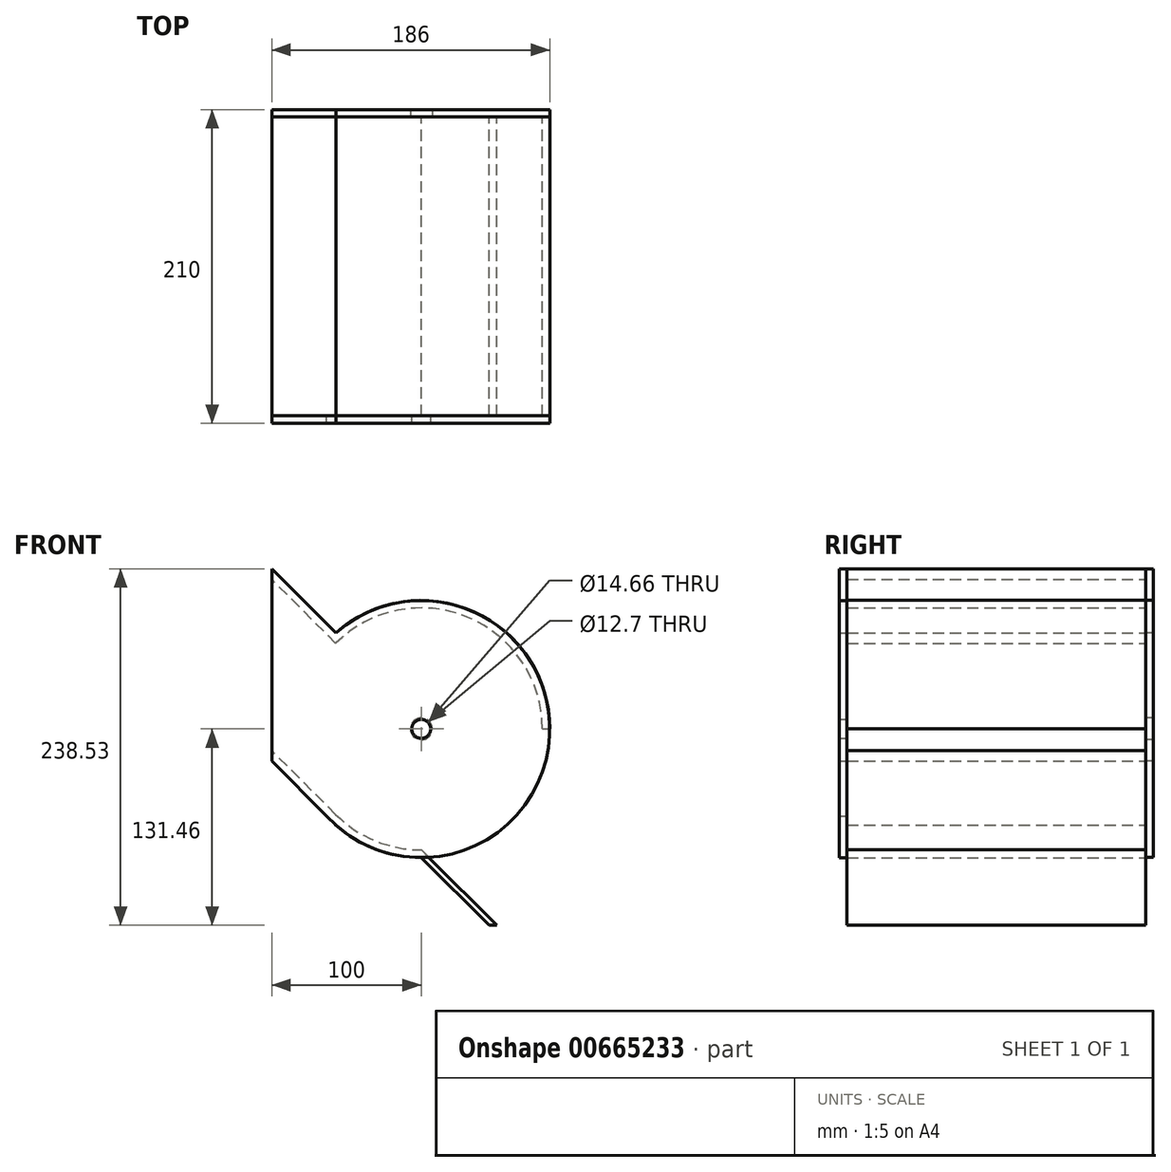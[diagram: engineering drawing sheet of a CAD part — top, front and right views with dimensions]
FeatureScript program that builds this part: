
annotation { "Feature Type Name" : "Feature", "Feature Type Description" : "" }
export const myFeature = defineFeature(function(context is Context, id is Id, definition is map)
    precondition{}
    {
        {
            var Q0;
            Q0=qCreatedBy(makeId("Front.planeOp"),FACE);
            var sketch = newSketch(context, id + "F0", { "sketchPlane" : qUnion([Q0])});
            skArc(sketch, "E0", {"start": v(81, 0) * mm, "mid": v(31, 74.83) * mm, "end": v(-57.28, 57.28) * mm});
            skLineSegment(sketch, "E1", {"start": v(0, 0) * mm, "end": v(0, -81) * mm});
            skPoint(sketch, "E2.visualSharp", {"position": v(0, -81) * mm});
            skArc(sketch, "E3", {"start": v(0, -81) * mm, "mid": v(-31, -74.83) * mm, "end": v(-57.28, -57.28) * mm});
            skLineSegment(sketch, "E4", {"start": v(-57.28, -57.28) * mm, "end": v(-100, -14.55) * mm});
            skLineSegment(sketch, "E5", {"start": v(81, 0) * mm, "end": v(86, 0) * mm});
            skArc(sketch, "E6", {"start": v(86, 0) * mm, "mid": v(35.2, 78.46) * mm, "end": v(-57.17, 64.24) * mm});
            skLineSegment(sketch, "E7", {"start": v(-100, -21.62) * mm, "end": v(-57.28, -64.35) * mm});
            skArc(sketch, "E8", {"start": v(-57.28, -64.35) * mm, "mid": v(-30.64, -80.51) * mm, "end": v(0, -86.15) * mm});
            skLineSegment(sketch, "E9", {"start": v(0, -81) * mm, "end": v(50.46, -131.46) * mm});
            skLineSegment(sketch, "E10", {"start": v(0, -86.15) * mm, "end": v(45.32, -131.46) * mm});
            skLineSegment(sketch, "E11", {"start": v(45.32, -131.46) * mm, "end": v(50.46, -131.46) * mm});
            skLineSegment(sketch, "E12", {"start": v(0, 0) * mm, "end": v(-100, 0) * mm, "construction": true});
            skLineSegment(sketch, "E13", {"start": v(-100, 0) * mm, "end": v(-100, 100) * mm, "construction": true});
            skLineSegment(sketch, "E14", {"start": v(-100, 100) * mm, "end": v(-100, 107.07) * mm});
            skLineSegment(sketch, "E15", {"start": v(-100, 107.07) * mm, "end": v(-57.17, 64.24) * mm});
            skLineSegment(sketch, "E16", {"start": v(-57.28, 57.28) * mm, "end": v(-100, 100) * mm});
            skLineSegment(sketch, "E17", {"start": v(-100, 0) * mm, "end": v(-100, -31.16) * mm, "construction": true});
            skLineSegment(sketch, "E18", {"start": v(-100, -14.55) * mm, "end": v(-100, -21.62) * mm});
            skSolve(sketch);
        }
        {
            var Q0;
            Q0=qSketchRegion(id+"F0",true);
            extrude(context, id + "F1", {"entities" : qUnion([Q0]), "depth" : 200 * mm});
        }
        {
            var Q0;
            Q0=qCreatedBy(makeId("Front.planeOp"),FACE);
            var sketch = newSketch(context, id + "F2", { "sketchPlane" : qUnion([Q0])});
            skCircle(sketch, "E19", {"center": v(0, 0) * mm, "radius": 86 * mm});
            skLineSegment(sketch, "E20", {"start": v(0, 0) * mm, "end": v(-100, 0) * mm});
            skLineSegment(sketch, "E21", {"start": v(-100, 0) * mm, "end": v(-100, -43.24) * mm, "construction": true});
            skLineSegment(sketch, "E22", {"start": v(-100, 0) * mm, "end": v(-100, 141.76) * mm, "construction": true});
            skLineSegment(sketch, "E23", {"start": v(-57.18, 64.24) * mm, "end": v(-100, 107.06) * mm});
            skLineSegment(sketch, "E24", {"start": v(-100, -21.62) * mm, "end": v(-60.81, -60.81) * mm});
            skLineSegment(sketch, "E25", {"start": v(-100, 107.06) * mm, "end": v(-100, -21.62) * mm});
            skLineSegment(sketch, "E26", {"start": v(0, 0) * mm, "end": v(0, -86) * mm});
            skLineSegment(sketch, "E27", {"start": v(0, 0) * mm, "end": v(-60.81, -60.81) * mm, "construction": true});
            skCircle(sketch, "E28", {"center": v(0, 0) * mm, "radius": 7.33 * mm});
            skSolve(sketch);
        }
        {
            var Q0;
            Q0=qSketchRegion(id+"F2",true);
            extrude(context, id + "F3", {"entities" : qUnion([Q0]), "oppositeDirection" : true, "depth" : 5 * mm});
        }
        {
            var Q0;
            Q0=qCreatedBy(makeId("Front.planeOp"),FACE);
            cPlane(context, id + "F4", {"entities" : qUnion([Q0]), "cplaneType" : CPlaneType.OFFSET, "offset" : 200 * mm, "width" : 150 * mm, "height" : 150 * mm});
        }
        {
            var Q0;
            Q0=qCreatedBy(id+"F4.planeOp",FACE);
            var sketch = newSketch(context, id + "F5", { "sketchPlane" : qUnion([Q0])});
            skCircle(sketch, "E29", {"center": v(0, -0.12) * mm, "radius": 86 * mm});
            skLineSegment(sketch, "E30", {"start": v(0, -0.12) * mm, "end": v(-100, -0.12) * mm});
            skLineSegment(sketch, "E31", {"start": v(-100, -0.12) * mm, "end": v(-100, -43.14) * mm, "construction": true});
            skLineSegment(sketch, "E32", {"start": v(-100, -0.12) * mm, "end": v(-100, 130.25) * mm, "construction": true});
            skLineSegment(sketch, "E33", {"start": v(-57.12, 64.18) * mm, "end": v(-100, 107.06) * mm});
            skLineSegment(sketch, "E34", {"start": v(-100, -21.63) * mm, "end": v(-58.14, -63.48) * mm});
            skLineSegment(sketch, "E35", {"start": v(-100, 107.06) * mm, "end": v(-100, -21.63) * mm});
            skLineSegment(sketch, "E36", {"start": v(0, -0.12) * mm, "end": v(0, -86.12) * mm});
            skCircle(sketch, "E37", {"center": v(0, 0) * mm, "radius": 6.35 * mm});
            skSolve(sketch);
        }
        {
            var Q0;
            Q0=qSketchRegion(id+"F5",true);
            extrude(context, id + "F6", {"entities" : qUnion([Q0]), "depth" : 5 * mm});
        }
    });
